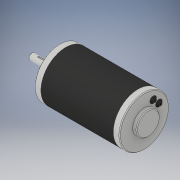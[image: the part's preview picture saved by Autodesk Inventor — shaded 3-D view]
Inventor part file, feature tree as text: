
AUTODESK INVENTOR PART (.ipt)
format: ipt  version: 2019 (Build 230136000, 136)  size: 161,792 bytes
history: native  units: in
note: dims shown in document units (in); Inventor stores cm internally (conversion verified against a paired STEP export)
features: chamfer x1
ambient origin geometry x8: Origin, YZ Plane, XZ Plane, XY Plane, X Axis, Y Axis, Z Axis, Center Point
bodies: Solid1 (feature_tree)
feature tree (1):
  chamfer  "Chamfer3"  [1 undecoded]
note: 1 required parameter value undecoded (feature->parameter linkage not recoverable at this tier; creation-order binding heuristic only, values carry confidence <= 0.55)
